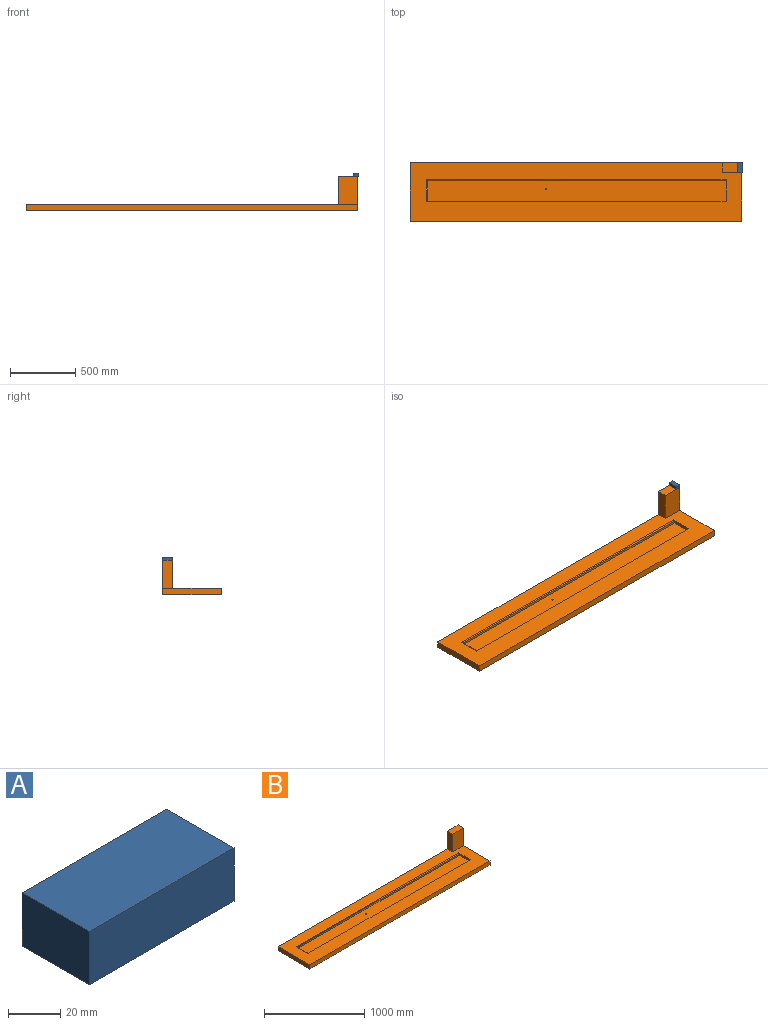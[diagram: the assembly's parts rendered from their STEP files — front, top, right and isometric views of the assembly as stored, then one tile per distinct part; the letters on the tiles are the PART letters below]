
ASSEMBLY  parts=2 mates=1
PART A: 6 faces, bbox 78.6x36.4x25 mm
  f0: plane 78.6x25mm, normal (0,1,0), area 1964.9mm2, adj f1,f3,f4,f5
  f1: plane 36.39x25mm, normal (-1,0,0), area 909.8mm2, adj f0,f2,f4,f5
  f2: plane 78.6x25mm, normal (0,-1,0), area 1964.9mm2, adj f1,f3,f4,f5
  f3: plane 36.39x25mm, normal (1,0,0), area 909.8mm2, adj f0,f2,f4,f5
  f4: plane 78.6x36.39mm, normal (0,0,1), area 2860.4mm2, adj f0,f1,f2,f3
  f5: plane 78.6x36.39mm, normal (0,0,-1), area 2860.4mm2, adj f0,f1,f2,f3
PART B: 20 faces, bbox 2540x450x265 mm
  f0: plane 2540x450mm, normal (0,0,1), area 752237.5mm2, adj f1,f2,f3,f4,f8,f9,f11,f12
  f1: plane 2540x265mm, normal (0,1,0), area 159838.5mm2, adj f0,f2,f4,f5,f15,f17
  f2: plane 450x50mm, normal (-1,0,0), area 22500mm2, adj f0,f1,f3,f5
  f3: plane 2540x50mm, normal (0,-1,0), area 127000mm2, adj f0,f2,f4,f5
  f4: plane 450x265mm, normal (1,0,0), area 38674.2mm2, adj f0,f1,f3,f5,f16,f17
  f5: plane 2540x450mm, normal (0,0,-1), area 1142980.4mm2, adj f1,f2,f3,f4,f18
  f6: plane 2278.5x17mm, normal (0,-1,0), area 38734.5mm2, adj f9,f10,f11,f13
  f7: plane 149.3x17mm, normal (1,0,0), area 2538mm2, adj f8,f10,f12,f13
  f8: plane 2294.5x25mm, normal (0,1,0), area 57176.2mm2, adj f0,f7,f9,f10,f12
  f9: plane 165.3x25mm, normal (-1,0,0), area 3946.1mm2, adj f0,f6,f8,f10,f11
  f10: plane 2286.5x157.3mm, normal (0,0,1), area 359565.7mm2, adj f6,f7,f8,f9,f13,f19
  f11: cylinder r=8mm len=2294.5mm, axis (1,0,0), area 28705.5mm2, adj f0,f6,f9,f14
  f12: cylinder r=8mm len=165.3mm, axis (0,1,0), area 1949.2mm2, adj f0,f7,f8,f14
  f13: cylinder r=8mm len=17mm, axis (0,0,1), area 213.6mm2, adj f6,f7,f10,f14
  f14: bspline ~16x16mm, area 120.9mm2, adj f11,f12,f13
  f15: plane 215x75.23mm, normal (-1,0,0), area 16174.2mm2, adj f0,f1,f16,f17
  f16: plane 215x152.74mm, normal (0,-1,0), area 32838.5mm2, adj f0,f4,f15,f17
  f17: plane 152.74x75.23mm, normal (0,0,1), area 11490.2mm2, adj f1,f4,f15,f16
  f18: cylinder r=2.5mm len=22.5mm, axis (0,0,1), area 353.4mm2, adj f5,f19
  f19: cone r=2.5mm half-angle=45deg, axis (0,0,1), area 83.3mm2, adj f10,f18
PLACE A rot(axis=(0,0,1),90deg) t=(2489.6,251.53,265)mm
PLACE B at identity fixed
MATE fastened A.f5 <-> B.f17  axis (0,0,-1) through (2485.7,262.31,265)mm
